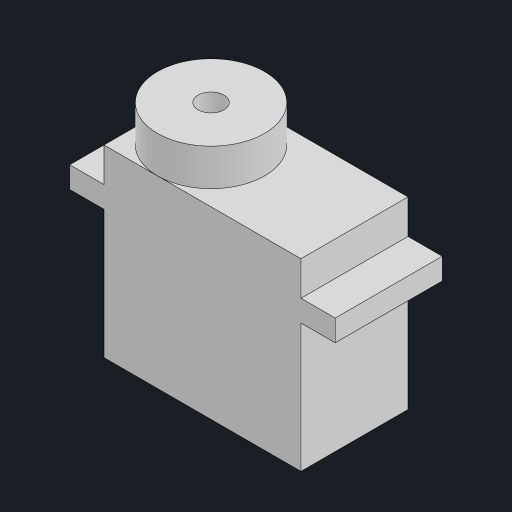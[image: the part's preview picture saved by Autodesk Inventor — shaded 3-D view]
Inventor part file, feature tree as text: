
AUTODESK INVENTOR PART (.ipt)
format: ipt  version: 2023 (Build 270158000, 158)  size: 129,024 bytes
history: native  units: in
note: dims shown in document units (in); Inventor stores cm internally (conversion verified against a paired STEP export)
features: sketch x5, extrude x4, other x1, hole x1
ambient origin geometry x8: Origin, YZ Plane, XZ Plane, XY Plane, X Axis, Y Axis, Z Axis, Center Point
bodies: Body1 (feature_tree)
feature tree (11):
  other  "ソリッド1"
  sketch  "スケッチ1"
  extrude  "押し出し1"  Depth=0.9055in
  extrude  "押し出し2"  Depth=0.4921in
  extrude  "押し出し3"  Depth=0.5906in TaperAngle=0.0deg
  extrude  "押し出し4"  Depth=0.1575in
  hole  "穴1"  [1 undecoded]
  sketch  "スケッチ2"
  sketch  "スケッチ3"
  sketch  "スケッチ4"
  sketch  "スケッチ5"
note: 1 required parameter value undecoded (feature->parameter linkage not recoverable at this tier; creation-order binding heuristic only, values carry confidence <= 0.55)
